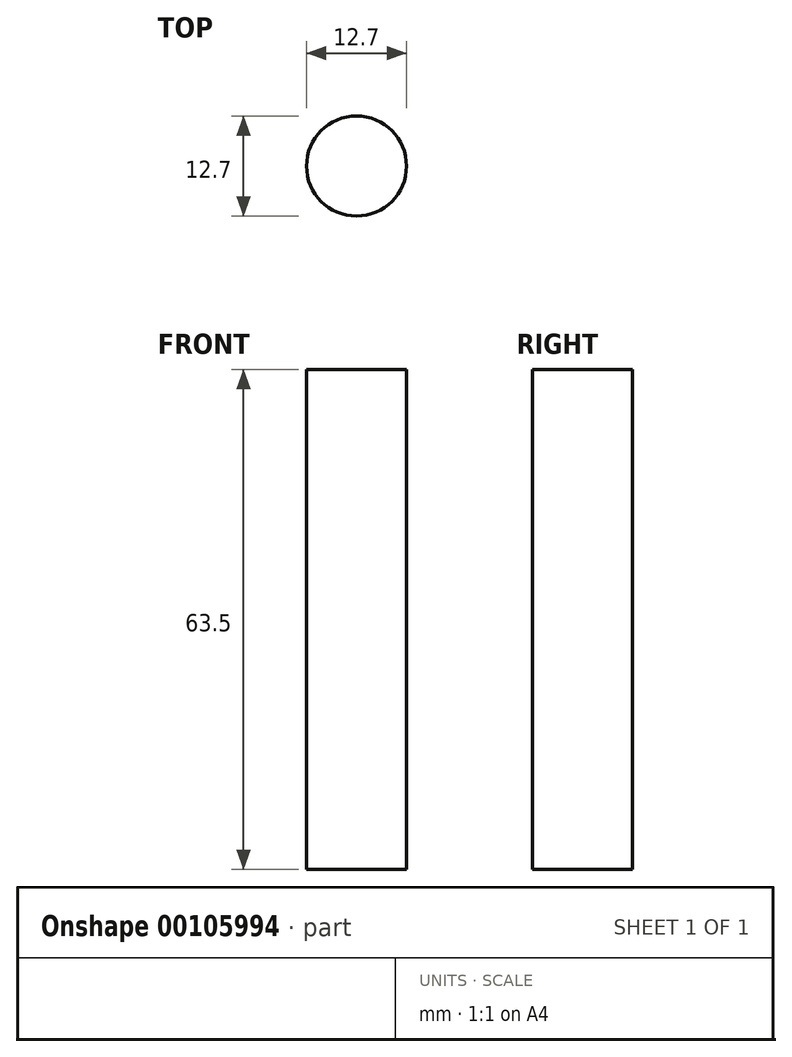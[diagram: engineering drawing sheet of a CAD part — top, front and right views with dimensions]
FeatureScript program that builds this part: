
annotation { "Feature Type Name" : "Feature", "Feature Type Description" : "" }
export const myFeature = defineFeature(function(context is Context, id is Id, definition is map)
    precondition{}
    {
        {
            var Q0;
            Q0=qCreatedBy(makeId("Top.planeOp"),FACE);
            var sketch = newSketch(context, id + "F0", { "sketchPlane" : qUnion([Q0])});
            skCircle(sketch, "E0", {"center": v(0, 0) * mm, "radius": 6.35 * mm});
            skSolve(sketch);
        }
        {
            var Q0;
            Q0=makeQuery(id+"F0.imprint","IMPRINT",FACE,{"disambiguationData":[TD([[makeQuery(id+"F0.imprint","IMPRINT",EDGE,{"derivedFrom":sQuery(id+"F0.wireOp",EDGE,"E0")}),1.0]])]});
            extrude(context, id + "F1", {"entities" : qUnion([Q0]), "depth" : 63.5 * mm});
        }
    });
